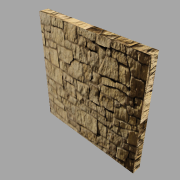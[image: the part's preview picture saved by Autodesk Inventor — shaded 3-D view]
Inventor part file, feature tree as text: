
AUTODESK INVENTOR PART (.ipt)
format: ipt  version: 2022.2 (Build 262287000, 287)  size: 128,512 bytes
history: native  units: in
note: dims shown in document units (in); Inventor stores cm internally (conversion verified against a paired STEP export)
features: extrude x1, sketch x1
ambient origin geometry x8: Origin, YZ Plane, XZ Plane, XY Plane, X Axis, Y Axis, Z Axis, Center Point
bodies: Solid1 (feature_tree)
feature tree (2):
  extrude  "Extrusion1"  Depth=12.0in
  sketch  "Sketch1"  dims[d0=12.0in d1=12.0in d2=1.0in d3=0.0in]
